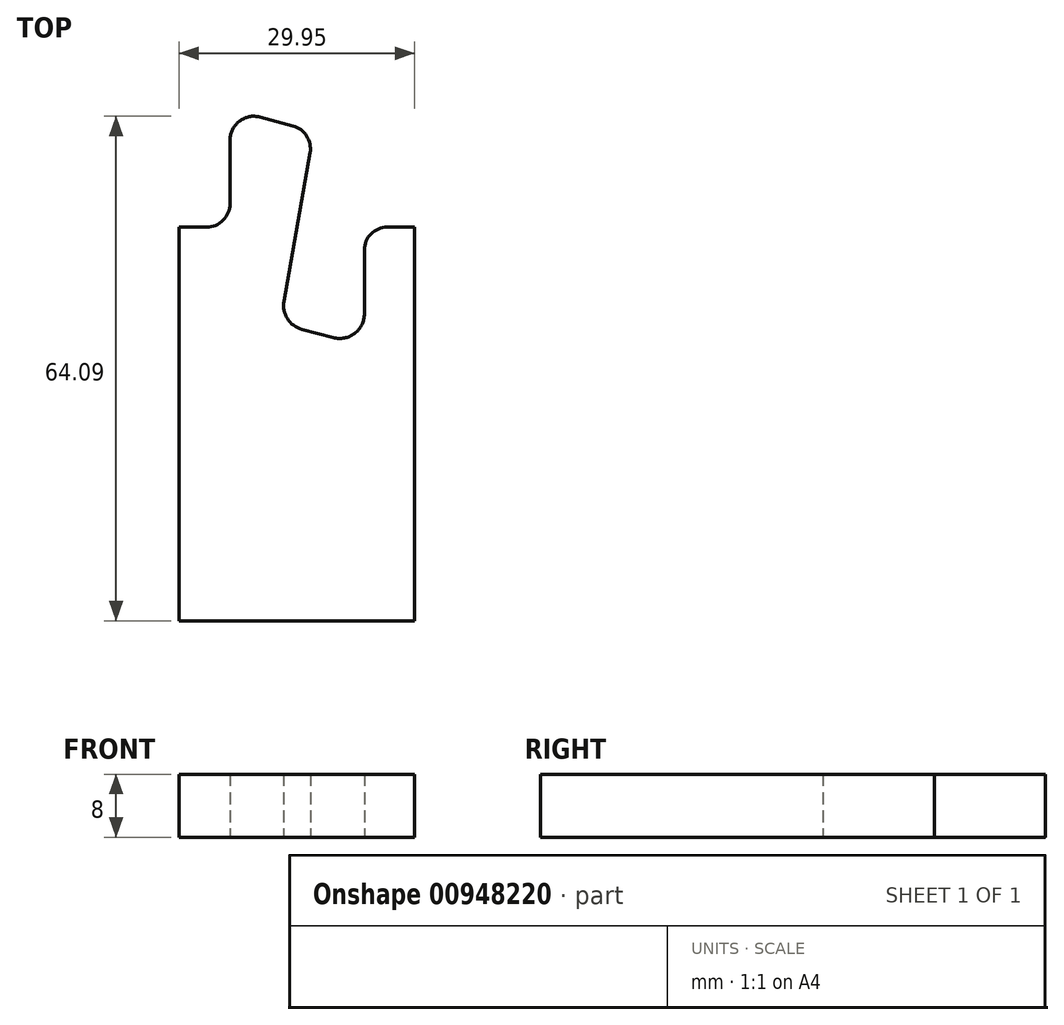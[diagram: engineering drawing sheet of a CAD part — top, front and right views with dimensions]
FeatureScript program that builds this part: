
annotation { "Feature Type Name" : "Feature", "Feature Type Description" : "" }
export const myFeature = defineFeature(function(context is Context, id is Id, definition is map)
    precondition{}
    {
        {
            var Q0;
            Q0=qCreatedBy(makeId("Top.planeOp"),FACE);
            var sketch = newSketch(context, id + "F0", { "sketchPlane" : qUnion([Q0])});
            skLineSegment(sketch, "E0", {"start": v(0, 0) * mm, "end": v(3.5, 0) * mm});
            skLineSegment(sketch, "E1", {"start": v(6.5, 3) * mm, "end": v(6.5, 11.1) * mm});
            skLineSegment(sketch, "E2", {"start": v(10.28, 13.99) * mm, "end": v(14.47, 12.86) * mm});
            skLineSegment(sketch, "E3", {"start": v(16.65, 9.45) * mm, "end": v(13.33, -9.38) * mm});
            skLineSegment(sketch, "E4", {"start": v(15.61, -12.97) * mm, "end": v(19.58, -14.04) * mm});
            skLineSegment(sketch, "E5", {"start": v(23.55, -11) * mm, "end": v(23.55, -2.9) * mm});
            skLineSegment(sketch, "E6", {"start": v(26.45, 0) * mm, "end": v(29.95, 0) * mm});
            skLineSegment(sketch, "E7", {"start": v(29.95, 0) * mm, "end": v(29.95, -50) * mm});
            skLineSegment(sketch, "E8", {"start": v(29.95, -50) * mm, "end": v(0, -50) * mm});
            skLineSegment(sketch, "E9", {"start": v(0, -50) * mm, "end": v(0, 0) * mm});
            skPoint(sketch, "E10.visualSharp", {"position": v(12.83, -12.23) * mm});
            skArc(sketch, "E10.filletArc", {"start": v(13.33, -9.38) * mm, "mid": v(13.77, -11.62) * mm, "end": v(15.61, -12.97) * mm});
            skPoint(sketch, "E11.visualSharp", {"position": v(23.55, -15.1) * mm});
            skArc(sketch, "E11.filletArc", {"start": v(19.58, -14.04) * mm, "mid": v(22.32, -13.5) * mm, "end": v(23.55, -11) * mm});
            skPoint(sketch, "E12.visualSharp", {"position": v(17.13, 12.15) * mm});
            skArc(sketch, "E12.filletArc", {"start": v(16.65, 9.45) * mm, "mid": v(16.22, 11.58) * mm, "end": v(14.47, 12.86) * mm});
            skPoint(sketch, "E13.visualSharp", {"position": v(6.5, 15) * mm});
            skArc(sketch, "E13.filletArc", {"start": v(10.28, 13.99) * mm, "mid": v(7.67, 13.47) * mm, "end": v(6.5, 11.1) * mm});
            skPoint(sketch, "E14.visualSharp", {"position": v(6.5, 0) * mm});
            skArc(sketch, "E14.filletArc", {"start": v(3.5, 0) * mm, "mid": v(5.62, 0.88) * mm, "end": v(6.5, 3) * mm});
            skPoint(sketch, "E15.visualSharp", {"position": v(23.55, 0) * mm});
            skArc(sketch, "E15.filletArc", {"start": v(26.45, 0) * mm, "mid": v(24.4, -0.85) * mm, "end": v(23.55, -2.9) * mm});
            skSolve(sketch);
        }
        {
            var Q0;
            Q0 = qSketchRegion(id + "F0", true);
            extrude(context, id + "F1", {"entities" : qUnion([Q0]), "depth" : 8 * mm, "offsetDistance" : 25 * mm});
        }
    });
